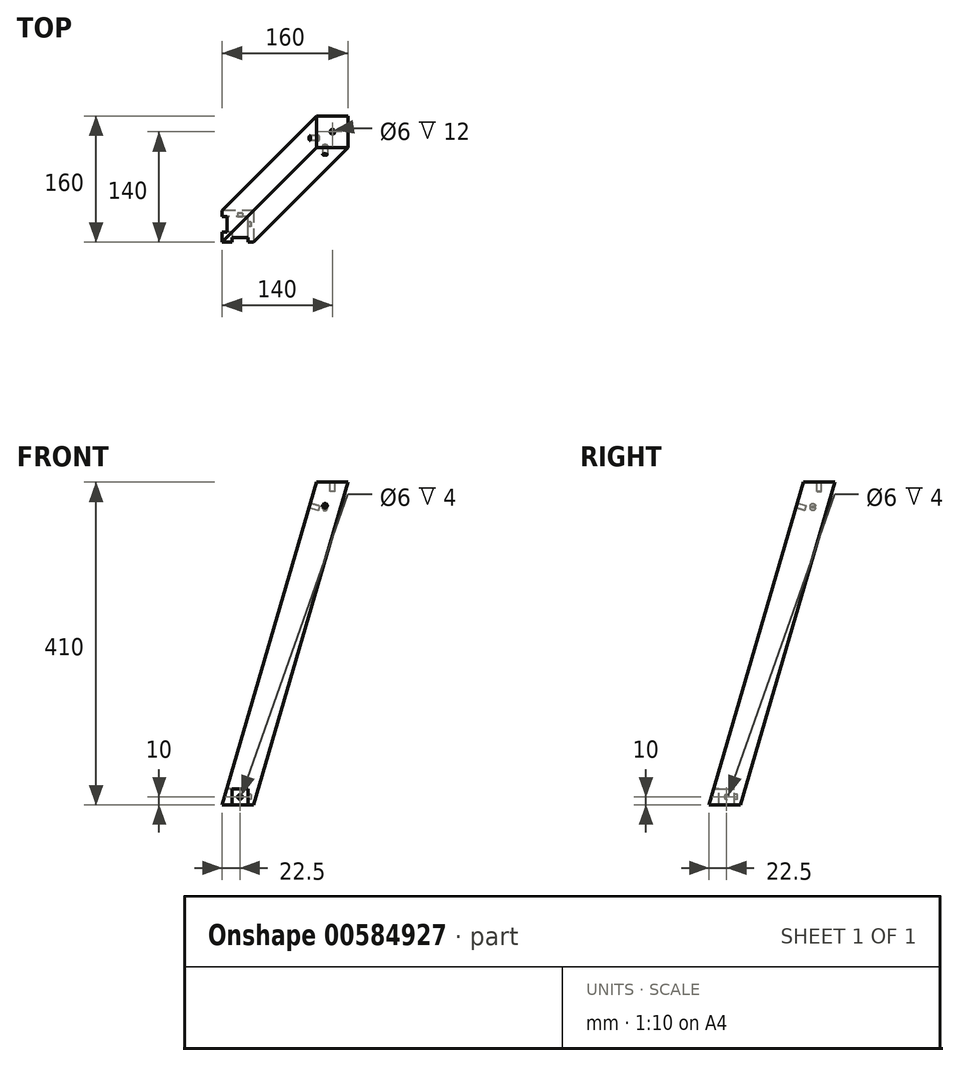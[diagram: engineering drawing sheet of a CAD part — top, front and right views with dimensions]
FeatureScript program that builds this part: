
annotation { "Feature Type Name" : "Feature", "Feature Type Description" : "" }
export const myFeature = defineFeature(function(context is Context, id is Id, definition is map)
    precondition{}
    {
        {
            var Q0;
            Q0=qCreatedBy(makeId("Top.planeOp"),FACE);
            var sketch = newSketch(context, id + "F0", { "sketchPlane" : qUnion([Q0])});
            skLineSegment(sketch, "E0.bottom", {"start": v(20, 20) * mm, "end": v(-20, 20) * mm});
            skLineSegment(sketch, "E0.top", {"start": v(20, -20) * mm, "end": v(-20, -20) * mm});
            skLineSegment(sketch, "E0.left", {"start": v(20, 20) * mm, "end": v(20, -20) * mm});
            skLineSegment(sketch, "E0.right", {"start": v(-20, 20) * mm, "end": v(-20, -20) * mm});
            skPoint(sketch, "E0.middle", {"position": v(0, 0) * mm});
            skSolve(sketch);
        }
        {
            var Q0;
            Q0=qCreatedBy(makeId("Top.planeOp"),FACE);
            cPlane(context, id + "F1", {"entities" : qUnion([Q0]), "cplaneType" : CPlaneType.OFFSET, "offset" : 410 * mm, "width" : 150 * mm, "height" : 150 * mm});
        }
        {
            var Q0;
            Q0=qCreatedBy(id+"F1.planeOp",FACE);
            var sketch = newSketch(context, id + "F2", { "sketchPlane" : qUnion([Q0])});
            skLineSegment(sketch, "E1.bottom", {"start": v(100, 100) * mm, "end": v(140, 100) * mm});
            skLineSegment(sketch, "E1.top", {"start": v(100, 140) * mm, "end": v(140, 140) * mm});
            skLineSegment(sketch, "E1.left", {"start": v(100, 100) * mm, "end": v(100, 140) * mm});
            skLineSegment(sketch, "E1.right", {"start": v(140, 100) * mm, "end": v(140, 140) * mm});
            skSolve(sketch);
        }
        {
            var Q0;
            Q0=makeQuery(id+"F0.imprint","IMPRINT",FACE,{"disambiguationData":[TD([[makeQuery(id+"F0.imprint","IMPRINT",EDGE,{"derivedFrom":sQuery(id+"F0.wireOp",EDGE,"E0.bottom")}),1.0]])]});
            var Q1;
            Q1=makeQuery(id+"F2.imprint","IMPRINT",FACE,{"disambiguationData":[TD([[makeQuery(id+"F2.imprint","IMPRINT",EDGE,{"derivedFrom":sQuery(id+"F2.wireOp",EDGE,"E1.bottom")}),1.0]])]});
            loft(context, id + "F3", {"sheetProfilesArray" : [{ "sheetProfileEntities" : qUnion([Q0]) }, { "sheetProfileEntities" : qUnion([Q1]) }]});
        }
        {
            var Q0;
            Q0=makeQuery(id+"F3.opLoft","SWEPT_FACE",FACE,{"disambiguationData":[OSD([sQuery(id+"F0.wireOp",EDGE,"E0.bottom"),sQuery(id+"F0.wireOp",EDGE,"E0.top"),sQuery(id+"F0.wireOp",EDGE,"E0.right"),sQuery(id+"F2.wireOp",EDGE,"E1.bottom"),sQuery(id+"F2.wireOp",EDGE,"E1.top"),sQuery(id+"F2.wireOp",EDGE,"E1.left")])]});
            var sketch = newSketch(context, id + "F4", { "sketchPlane" : qUnion([Q0])});
            skCircle(sketch, "E2", {"center": v(-112.01, 390.38) * mm, "radius": 3 * mm});
            skSolve(sketch);
        }
        {
            var Q0;
            Q0 = qSketchRegion(id + "F4", true);
            extrude(context, id + "F5", {"entities" : qUnion([Q0]), "operationType" : NewBodyOperationType.REMOVE, "oppositeDirection" : true, "depth" : 12 * mm, "offsetDistance" : 25 * mm});
        }
        {
            var Q0;
            Q0=makeQuery(id+"F3.opLoft","SWEPT_FACE",FACE,{"disambiguationData":[OSD([sQuery(id+"F0.wireOp",EDGE,"E0.top"),sQuery(id+"F0.wireOp",EDGE,"E0.left"),sQuery(id+"F0.wireOp",EDGE,"E0.right"),sQuery(id+"F2.wireOp",EDGE,"E1.bottom"),sQuery(id+"F2.wireOp",EDGE,"E1.left"),sQuery(id+"F2.wireOp",EDGE,"E1.right")])]});
            var sketch = newSketch(context, id + "F6", { "sketchPlane" : qUnion([Q0])});
            skCircle(sketch, "E3", {"center": v(110.46, 390.38) * mm, "radius": 3 * mm});
            skSolve(sketch);
        }
        {
            var Q0;
            Q0 = qSketchRegion(id + "F6", true);
            extrude(context, id + "F7", {"entities" : qUnion([Q0]), "operationType" : NewBodyOperationType.REMOVE, "oppositeDirection" : true, "depth" : 12 * mm, "offsetDistance" : 25 * mm});
        }
        {
            var Q0;
            Q0=makeQuery(id+"F3.opLoft","CAP_FACE",FACE,{"disambiguationData":[OSD([makeQuery(id+"F2.imprint","IMPRINT",FACE,{"disambiguationData":[TD([[makeQuery(id+"F2.imprint","IMPRINT",EDGE,{"derivedFrom":sQuery(id+"F2.wireOp",EDGE,"E1.bottom")}),1.0]])]})])],"isStart":true});
            var sketch = newSketch(context, id + "F8", { "sketchPlane" : qUnion([Q0])});
            skCircle(sketch, "E4", {"center": v(120, 120) * mm, "radius": 3 * mm});
            skSolve(sketch);
        }
        {
            var Q0;
            Q0=makeQuery(id+"F8.imprint","IMPRINT",FACE,{"disambiguationData":[TD([[makeQuery(id+"F8.imprint","IMPRINT",EDGE,{"derivedFrom":sQuery(id+"F8.wireOp",EDGE,"E4")}),1.0]])]});
            extrude(context, id + "F9", {"entities" : qUnion([Q0]), "operationType" : NewBodyOperationType.REMOVE, "oppositeDirection" : true, "depth" : 12 * mm, "offsetDistance" : 25 * mm});
        }
        {
            var Q0;
            Q0=qCreatedBy(makeId("Right.planeOp"),FACE);
            cPlane(context, id + "F10", {"entities" : qUnion([Q0]), "cplaneType" : CPlaneType.OFFSET, "offset" : 20 * mm, "oppositeDirection" : true, "width" : 150 * mm, "height" : 150 * mm});
        }
        {
            var Q0;
            Q0=qCreatedBy(id+"F10.planeOp",FACE);
            var sketch = newSketch(context, id + "F11", { "sketchPlane" : qUnion([Q0])});
            skLineSegment(sketch, "E5.bottom", {"start": v(-7.5, 0) * mm, "end": v(12.5, 0) * mm});
            skLineSegment(sketch, "E5.top", {"start": v(-7.5, 20) * mm, "end": v(12.5, 20) * mm});
            skLineSegment(sketch, "E5.left", {"start": v(-7.5, 0) * mm, "end": v(-7.5, 20) * mm});
            skLineSegment(sketch, "E5.right", {"start": v(12.5, 0) * mm, "end": v(12.5, 20) * mm});
            skSolve(sketch);
        }
        {
            var Q0;
            Q0=makeQuery(id+"F11.imprint","IMPRINT",FACE,{"disambiguationData":[TD([[makeQuery(id+"F11.imprint","IMPRINT",EDGE,{"derivedFrom":sQuery(id+"F11.wireOp",EDGE,"E5.bottom")}),1.0]])]});
            extrude(context, id + "F12", {"entities" : qUnion([Q0]), "operationType" : NewBodyOperationType.REMOVE, "depth" : 32.5 * mm, "offsetDistance" : 25 * mm});
        }
        {
            var Q0;
            Q0=qCreatedBy(makeId("Front.planeOp"),FACE);
            cPlane(context, id + "F13", {"entities" : qUnion([Q0]), "cplaneType" : CPlaneType.OFFSET, "offset" : 20 * mm, "width" : 150 * mm, "height" : 150 * mm});
        }
        {
            var Q0;
            Q0=qCreatedBy(id+"F13.planeOp",FACE);
            var sketch = newSketch(context, id + "F14", { "sketchPlane" : qUnion([Q0])});
            skLineSegment(sketch, "E6.bottom", {"start": v(-7.5, 0) * mm, "end": v(12.5, 0) * mm});
            skLineSegment(sketch, "E6.top", {"start": v(-7.5, 20) * mm, "end": v(12.5, 20) * mm});
            skLineSegment(sketch, "E6.left", {"start": v(-7.5, 0) * mm, "end": v(-7.5, 20) * mm});
            skLineSegment(sketch, "E6.right", {"start": v(12.5, 0) * mm, "end": v(12.5, 20) * mm});
            skSolve(sketch);
        }
        {
            var Q0;
            Q0=makeQuery(id+"F14.imprint","IMPRINT",FACE,{"disambiguationData":[TD([[makeQuery(id+"F14.imprint","IMPRINT",EDGE,{"derivedFrom":sQuery(id+"F14.wireOp",EDGE,"E6.bottom")}),1.0]])]});
            extrude(context, id + "F15", {"entities" : qUnion([Q0]), "operationType" : NewBodyOperationType.REMOVE, "oppositeDirection" : true, "depth" : 32.5 * mm, "offsetDistance" : 25 * mm});
        }
        {
            var Q0;
            Q0=makeQuery(id+"F12.boolean.opBoolean","COPY",FACE,{"derivedFrom":makeQuery(id+"F12.opExtrude","SWEPT_FACE",FACE,{"disambiguationData":[OSD([sQuery(id+"F11.wireOp",EDGE,"E5.right")])]})});
            var sketch = newSketch(context, id + "F16", { "sketchPlane" : qUnion([Q0])});
            skCircle(sketch, "E7", {"center": v(2.5, 10) * mm, "radius": 3 * mm});
            skSolve(sketch);
        }
        {
            var Q0;
            Q0=makeQuery(id+"F16.imprint","IMPRINT",FACE,{"disambiguationData":[TD([[makeQuery(id+"F16.imprint","IMPRINT",EDGE,{"derivedFrom":sQuery(id+"F16.wireOp",EDGE,"E7")}),1.0]])]});
            extrude(context, id + "F17", {"entities" : qUnion([Q0]), "operationType" : NewBodyOperationType.REMOVE, "oppositeDirection" : true, "depth" : 4 * mm, "offsetDistance" : 25 * mm});
        }
        {
            var Q0;
            Q0=makeQuery(id+"F15.boolean.opBoolean","MERGE",FACE,{"derivedFrom":[makeQuery(id+"F12.boolean.opBoolean","COPY",FACE,{"derivedFrom":makeQuery(id+"F12.opExtrude","CAP_FACE",FACE,{"disambiguationData":[OSD([sQuery(id+"F11.wireOp",EDGE,"E5.bottom"),sQuery(id+"F11.wireOp",EDGE,"E5.top"),sQuery(id+"F11.wireOp",EDGE,"E5.left"),sQuery(id+"F11.wireOp",EDGE,"E5.right")])],"isStart":false})}),makeQuery(id+"F15.opExtrude","SWEPT_FACE",FACE,{"disambiguationData":[OSD([sQuery(id+"F14.wireOp",EDGE,"E6.right")])]})]});
            var sketch = newSketch(context, id + "F18", { "sketchPlane" : qUnion([Q0])});
            skCircle(sketch, "E8", {"center": v(-2.5, 10) * mm, "radius": 3 * mm});
            skSolve(sketch);
        }
        {
            var Q0;
            Q0=makeQuery(id+"F18.imprint","IMPRINT",FACE,{"disambiguationData":[TD([[makeQuery(id+"F18.imprint","IMPRINT",EDGE,{"derivedFrom":sQuery(id+"F18.wireOp",EDGE,"E8")}),1.0]])]});
            extrude(context, id + "F19", {"entities" : qUnion([Q0]), "operationType" : NewBodyOperationType.REMOVE, "oppositeDirection" : true, "depth" : 4 * mm, "offsetDistance" : 25 * mm});
        }
    });
